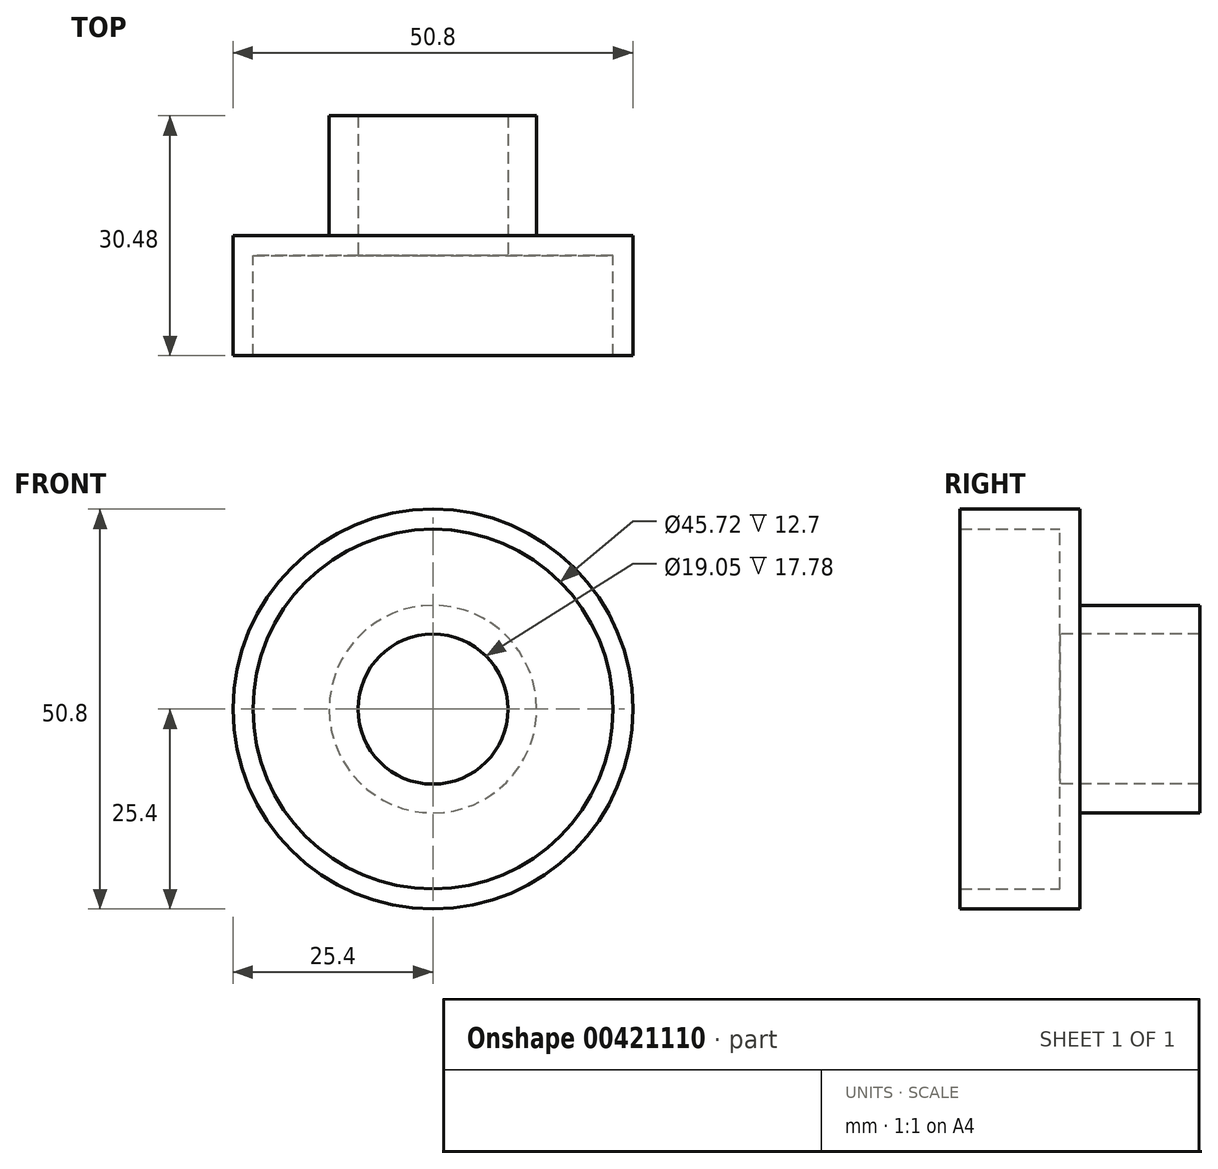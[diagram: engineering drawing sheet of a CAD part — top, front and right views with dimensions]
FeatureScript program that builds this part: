
annotation { "Feature Type Name" : "Feature", "Feature Type Description" : "" }
export const myFeature = defineFeature(function(context is Context, id is Id, definition is map)
    precondition{}
    {
        {
            var Q0;
            Q0=qCreatedBy(makeId("Front.planeOp"),FACE);
            var sketch = newSketch(context, id + "F0", { "sketchPlane" : qUnion([Q0])});
            skCircle(sketch, "E0", {"center": v(0, 0) * mm, "radius": 22.86 * mm});
            skCircle(sketch, "E1", {"center": v(0, 0) * mm, "radius": 25.4 * mm});
            skSolve(sketch);
        }
        {
            var Q0;
            Q0 = qSketchRegion(id + "F0", true);
            extrude(context, id + "F1", {"entities" : qUnion([Q0]), "depth" : 3.8 * mm});
        }
        {
            var Q0;
            Q0 = qSketchRegion(id + "F0", true);
            extrude(context, id + "F2", {"entities" : qUnion([Q0]), "operationType" : NewBodyOperationType.ADD, "depth" : 12.7 * mm});
        }
        {
            var Q0;
            Q0=makeQuery(id+"F1.opExtrude","CAP_FACE",FACE,{"disambiguationData":[OSD([sQuery(id+"F0.wireOp",EDGE,"E1"),sQuery(id+"F0.wireOp",EDGE,"E1")])],"isStart":true});
            var sketch = newSketch(context, id + "F3", { "sketchPlane" : qUnion([Q0])});
            skCircle(sketch, "E2", {"center": v(0, 0) * mm, "radius": 22.86 * mm});
            skCircle(sketch, "E3", {"center": v(0, 0) * mm, "radius": 13.18 * mm});
            skCircle(sketch, "E4.0", {"center": v(0, 0) * mm, "radius": 9.53 * mm});
            skSolve(sketch);
        }
        {
            var Q0;
            Q0=makeQuery(id+"F3.imprint","IMPRINT",FACE,{"disambiguationData":[TD([[makeQuery(id+"F3.imprint","IMPRINT",EDGE,{"derivedFrom":sQuery(id+"F3.wireOp",EDGE,"E3")}),-1.0]])]});
            var Q1;
            Q1=makeQuery(id+"F3.imprint","IMPRINT",FACE,{"disambiguationData":[TD([[makeQuery(id+"F3.imprint","IMPRINT",EDGE,{"derivedFrom":sQuery(id+"F3.wireOp",EDGE,"E2")}),1.0]])]});
            extrude(context, id + "F4", {"entities" : qUnion([Q0, Q1]), "operationType" : NewBodyOperationType.ADD, "depth" : 2.54 * mm});
        }
        {
            var Q0;
            Q0=makeQuery(id+"F3.imprint","IMPRINT",FACE,{"disambiguationData":[TD([[makeQuery(id+"F3.imprint","IMPRINT",EDGE,{"derivedFrom":sQuery(id+"F3.wireOp",EDGE,"E3")}),1.0]])]});
            extrude(context, id + "F5", {"entities" : qUnion([Q0]), "operationType" : NewBodyOperationType.ADD, "depth" : 17.78 * mm});
        }
    });
